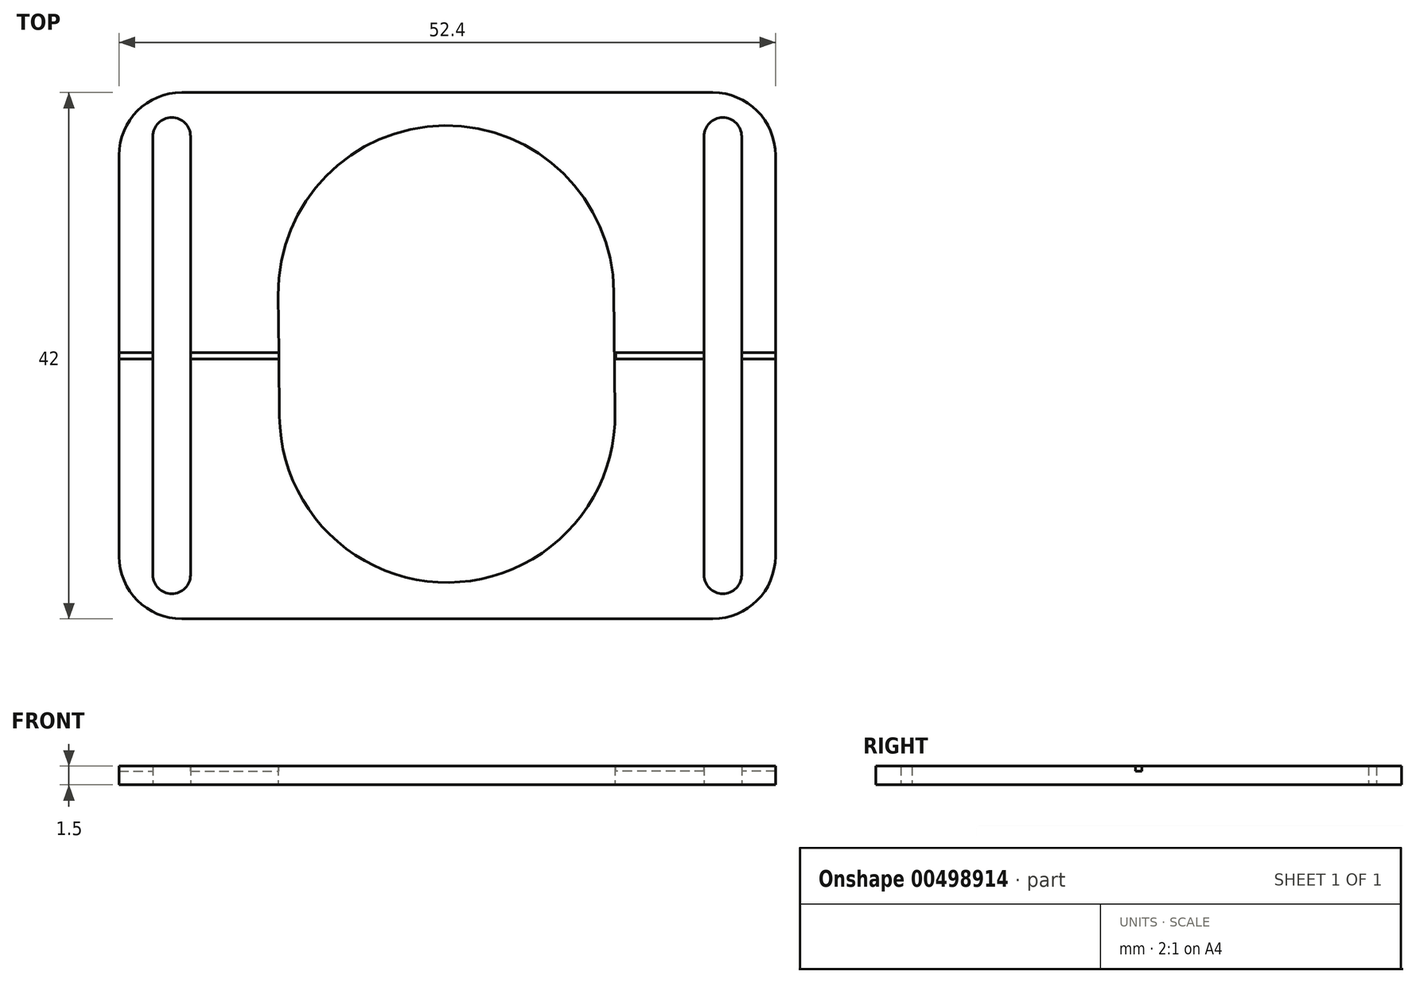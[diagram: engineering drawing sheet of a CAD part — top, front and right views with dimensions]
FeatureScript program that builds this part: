
annotation { "Feature Type Name" : "Feature", "Feature Type Description" : "" }
export const myFeature = defineFeature(function(context is Context, id is Id, definition is map)
    precondition{}
    {
        {
            var Q0;
            Q0=qCreatedBy(makeId("Top.planeOp"),FACE);
            var sketch = newSketch(context, id + "F0", { "sketchPlane" : qUnion([Q0])});
            skPoint(sketch, "E0.0", {"position": v(-35, -49.5) * mm});
            skPoint(sketch, "E1.0", {"position": v(35, -49.5) * mm});
            skLineSegment(sketch, "E2", {"start": v(-35, 25.5) * mm, "end": v(35, 25.5) * mm, "construction": true});
            skLineSegment(sketch, "E3.bottom", {"start": v(-32, -49.5) * mm, "end": v(-22, -49.5) * mm});
            skLineSegment(sketch, "E3.left", {"start": v(-35, -46.5) * mm, "end": v(-35, -44.8) * mm});
            skLineSegment(sketch, "E3.right", {"start": v(-19, -46.5) * mm, "end": v(-19, -45.44) * mm});
            skLineSegment(sketch, "E4.bottom", {"start": v(32, -49.5) * mm, "end": v(22, -49.5) * mm});
            skLineSegment(sketch, "E4.left", {"start": v(35, -46.5) * mm, "end": v(35, -44.8) * mm});
            skLineSegment(sketch, "E4.right", {"start": v(19, -46.5) * mm, "end": v(19, -45.44) * mm});
            skPoint(sketch, "E5.0", {"position": v(-19.7, -19.3) * mm});
            skPoint(sketch, "E6.0", {"position": v(19.7, -19.3) * mm});
            skArc(sketch, "E7", {"start": v(-30.65, -39.5) * mm, "mid": v(-31.62, -41.02) * mm, "end": v(-33.12, -42.02) * mm});
            skLineSegment(sketch, "E8", {"start": v(-18.8, -44.37) * mm, "end": v(-13.23, -29.76) * mm});
            skPoint(sketch, "E9.MirrorP", {"position": v(19.2, -19.2) * mm});
            skArc(sketch, "E10.MirrorCS", {"start": v(30.65, -39.5) * mm, "mid": v(31.62, -41.02) * mm, "end": v(33.12, -42.02) * mm});
            skLineSegment(sketch, "E11.MirrorCS", {"start": v(18.8, -44.37) * mm, "end": v(13.23, -29.76) * mm});
            skPoint(sketch, "E12.orphan", {"position": v(19, -39.5) * mm});
            skPoint(sketch, "E13.orphan", {"position": v(-19, -39.5) * mm});
            skPoint(sketch, "E14.visualSharp", {"position": v(-35, -42.32) * mm});
            skArc(sketch, "E14.filletArc", {"start": v(-33.12, -42.02) * mm, "mid": v(-34.48, -43.12) * mm, "end": v(-35, -44.8) * mm});
            skPoint(sketch, "E15.visualSharp", {"position": v(35, -42.32) * mm});
            skArc(sketch, "E15.filletArc", {"start": v(35, -44.8) * mm, "mid": v(34.48, -43.12) * mm, "end": v(33.12, -42.02) * mm});
            skArc(sketch, "E16.filletArc", {"start": v(32, -49.5) * mm, "mid": v(34.12, -48.62) * mm, "end": v(35, -46.5) * mm});
            skPoint(sketch, "E17.visualSharp", {"position": v(19, -49.5) * mm});
            skArc(sketch, "E17.filletArc", {"start": v(19, -46.5) * mm, "mid": v(19.88, -48.62) * mm, "end": v(22, -49.5) * mm});
            skPoint(sketch, "E18.visualSharp", {"position": v(-19, -49.5) * mm});
            skArc(sketch, "E18.filletArc", {"start": v(-22, -49.5) * mm, "mid": v(-19.88, -48.62) * mm, "end": v(-19, -46.5) * mm});
            skArc(sketch, "E19.filletArc", {"start": v(-35, -46.5) * mm, "mid": v(-34.12, -48.62) * mm, "end": v(-32, -49.5) * mm});
            skPoint(sketch, "E20.visualSharp", {"position": v(-19, -44.89) * mm});
            skArc(sketch, "E20.filletArc", {"start": v(-18.8, -44.37) * mm, "mid": v(-18.95, -44.9) * mm, "end": v(-19, -45.44) * mm});
            skPoint(sketch, "E21.visualSharp", {"position": v(19, -44.89) * mm});
            skArc(sketch, "E21.filletArc", {"start": v(19, -45.44) * mm, "mid": v(18.95, -44.9) * mm, "end": v(18.8, -44.37) * mm});
            skPoint(sketch, "E22.0", {"position": v(-32, 22.5) * mm});
            skPoint(sketch, "E23.0", {"position": v(-22, 22.5) * mm});
            skPoint(sketch, "E24.0", {"position": v(22, 22.5) * mm});
            skPoint(sketch, "E25.0", {"position": v(32, 22.5) * mm});
            skLineSegment(sketch, "E26.bottom", {"start": v(-32, 25.5) * mm, "end": v(-22, 25.5) * mm});
            skLineSegment(sketch, "E26.left", {"start": v(-35, 22.32) * mm, "end": v(-34.9, 20.58) * mm});
            skArc(sketch, "E27.filletArc", {"start": v(-34.9, 20.58) * mm, "mid": v(-34.34, 19.02) * mm, "end": v(-33.05, 18) * mm});
            skArc(sketch, "E28.filletArc", {"start": v(-32, 25.5) * mm, "mid": v(-34.18, 24.56) * mm, "end": v(-35, 22.32) * mm});
            skArc(sketch, "E29.filletArc", {"start": v(-19.63, 24.33) * mm, "mid": v(-20.68, 25.19) * mm, "end": v(-22, 25.5) * mm});
            skLineSegment(sketch, "E30", {"start": v(-33.05, 18) * mm, "end": v(-29.27, 16.41) * mm});
            skLineSegment(sketch, "E31.MirrorCS", {"start": v(35, 22.32) * mm, "end": v(34.9, 20.58) * mm});
            skArc(sketch, "E32.MirrorCS", {"start": v(19.63, 24.33) * mm, "mid": v(20.68, 25.19) * mm, "end": v(22, 25.5) * mm});
            skArc(sketch, "E33.MirrorCS", {"start": v(34.9, 20.58) * mm, "mid": v(34.34, 19.02) * mm, "end": v(33.05, 18) * mm});
            skArc(sketch, "E34.MirrorCS", {"start": v(32, 25.5) * mm, "mid": v(34.18, 24.56) * mm, "end": v(35, 22.32) * mm});
            skLineSegment(sketch, "E35.MirrorCS", {"start": v(32, 25.5) * mm, "end": v(22, 25.5) * mm});
            skLineSegment(sketch, "E36.MirrorCS", {"start": v(33.05, 18) * mm, "end": v(29.27, 16.41) * mm});
            skLineSegment(sketch, "E37", {"start": v(-15.68, 22.4) * mm, "end": v(15.68, 22.4) * mm});
            skLineSegment(sketch, "E38", {"start": v(-26.2, -26.85) * mm, "end": v(-26.2, 11.8) * mm});
            skLineSegment(sketch, "E39", {"start": v(-32, 22.5) * mm, "end": v(-22, 22.5) * mm, "construction": true});
            skCircle(sketch, "E40", {"center": v(-32, 22.5) * mm, "radius": 1.5 * mm});
            skCircle(sketch, "E41", {"center": v(32, 22.5) * mm, "radius": 1.5 * mm});
            skCircle(sketch, "E42", {"center": v(-32, -46.5) * mm, "radius": 1.5 * mm});
            skCircle(sketch, "E43", {"center": v(-22, -46.5) * mm, "radius": 1.5 * mm});
            skCircle(sketch, "E44", {"center": v(22, -46.5) * mm, "radius": 1.5 * mm});
            skCircle(sketch, "E45", {"center": v(32, -46.5) * mm, "radius": 1.5 * mm});
            skCircle(sketch, "E46", {"center": v(-22, 22.5) * mm, "radius": 1.5 * mm});
            skCircle(sketch, "E47", {"center": v(22, 22.5) * mm, "radius": 1.5 * mm});
            skCircle(sketch, "E48.0", {"center": v(-22, 0) * mm, "radius": 1.5 * mm, "construction": true});
            skCircle(sketch, "E49.0", {"center": v(-22, 10) * mm, "radius": 1.5 * mm, "construction": true});
            skCircle(sketch, "E50.0", {"center": v(-22, -10) * mm, "radius": 1.5 * mm, "construction": true});
            skArc(sketch, "E51.0.1.0", {"start": v(-23.5, -17.5) * mm, "mid": v(-22, -19) * mm, "end": v(-20.5, -17.5) * mm});
            skLineSegment(sketch, "E51.direction1", {"start": v(-22, -10) * mm, "end": v(3, -10) * mm, "construction": true});
            skLineSegment(sketch, "E51.direction2", {"start": v(-22, -10) * mm, "end": v(-22, -17.5) * mm, "construction": true});
            skArc(sketch, "E52.0.1.0", {"start": v(-20.5, 17.5) * mm, "mid": v(-22, 19) * mm, "end": v(-23.5, 17.5) * mm});
            skLineSegment(sketch, "E52.direction1", {"start": v(-22, 10) * mm, "end": v(3, 10) * mm, "construction": true});
            skLineSegment(sketch, "E52.direction2", {"start": v(-22, 10) * mm, "end": v(-22, 17.5) * mm, "construction": true});
            skLineSegment(sketch, "E53", {"start": v(-20.5, 17.5) * mm, "end": v(-20.5, -17.5) * mm});
            skLineSegment(sketch, "E54", {"start": v(-23.5, 17.5) * mm, "end": v(-23.5, -17.5) * mm});
            skArc(sketch, "E55.trimOffspring", {"start": v(-21.84, -16) * mm, "mid": v(-21.92, -16) * mm, "end": v(-22, -16) * mm});
            skLineSegment(sketch, "E56", {"start": v(-10.5, -26.94) * mm, "end": v(-3.06, -23.82) * mm});
            skLineSegment(sketch, "E57", {"start": v(3.15, -23.82) * mm, "end": v(10.5, -26.93) * mm});
            skPoint(sketch, "E58.orphan", {"position": v(-10.37, -22.5) * mm});
            skPoint(sketch, "E59.end.orphan", {"position": v(10.47, -22.53) * mm});
            skPoint(sketch, "E60.visualSharp", {"position": v(0.05, -22.51) * mm});
            skArc(sketch, "E60.filletArc", {"start": v(3.15, -23.82) * mm, "mid": v(0.05, -23.2) * mm, "end": v(-3.06, -23.82) * mm});
            skPoint(sketch, "E61.orphan", {"position": v(-26.2, 16.8) * mm});
            skPoint(sketch, "E62.trimOffspring.end.orphan", {"position": v(-19.2, 12.2) * mm});
            skLineSegment(sketch, "E63.trimOffspring", {"start": v(-26.52, -28.62) * mm, "end": v(-30.65, -39.5) * mm});
            skPoint(sketch, "E64.start.orphan", {"position": v(-19.2, -9.3) * mm});
            skPoint(sketch, "E65.trimOffspring.end.orphan", {"position": v(-9.7, -19.2) * mm});
            skPoint(sketch, "E66.orphan", {"position": v(9.2, -19.2) * mm});
            skLineSegment(sketch, "E67.MirrorCS", {"start": v(26.2, -26.85) * mm, "end": v(26.2, 11.8) * mm});
            skCircle(sketch, "E68.MirrorC", {"center": v(22, 10) * mm, "radius": 1.5 * mm, "construction": true});
            skLineSegment(sketch, "E69.MirrorCS", {"start": v(23.5, 17.5) * mm, "end": v(23.5, -17.5) * mm});
            skLineSegment(sketch, "E70.MirrorCS", {"start": v(22, -10) * mm, "end": v(22, -17.5) * mm, "construction": true});
            skLineSegment(sketch, "E71.MirrorCS", {"start": v(22, 10) * mm, "end": v(22, 17.5) * mm, "construction": true});
            skCircle(sketch, "E72.MirrorC", {"center": v(22, -10) * mm, "radius": 1.5 * mm, "construction": true});
            skArc(sketch, "E73.MirrorCS", {"start": v(20.5, 17.5) * mm, "mid": v(22, 19) * mm, "end": v(23.5, 17.5) * mm});
            skArc(sketch, "E74.MirrorCS", {"start": v(23.5, -17.5) * mm, "mid": v(22, -19) * mm, "end": v(20.5, -17.5) * mm});
            skLineSegment(sketch, "E75.MirrorCS", {"start": v(20.5, 17.5) * mm, "end": v(20.5, -17.5) * mm});
            skCircle(sketch, "E76.MirrorC", {"center": v(22, 0) * mm, "radius": 1.5 * mm, "construction": true});
            skLineSegment(sketch, "E77.trimOffspring", {"start": v(26.52, -28.62) * mm, "end": v(30.65, -39.5) * mm});
            skPoint(sketch, "E78.MirrorCS.end.orphan", {"position": v(22, -16) * mm});
            skPoint(sketch, "E78.MirrorCS.start.orphan", {"position": v(21.84, -16) * mm});
            skPoint(sketch, "E79.end.orphan", {"position": v(19.2, 12.2) * mm});
            skPoint(sketch, "E79.start.orphan", {"position": v(19.2, -9.2) * mm});
            skPoint(sketch, "E80.MirrorCS.end.orphan", {"position": v(19, 19.2) * mm});
            skPoint(sketch, "E81.MirrorCS.end.orphan", {"position": v(19, 21.46) * mm});
            skPoint(sketch, "E82.end.orphan", {"position": v(-19, 19.2) * mm});
            skPoint(sketch, "E26.right.end.orphan", {"position": v(-19, 21.46) * mm});
            skPoint(sketch, "E83.visualSharp", {"position": v(-26.2, -27.76) * mm});
            skArc(sketch, "E83.filletArc", {"start": v(-26.52, -28.62) * mm, "mid": v(-26.28, -27.75) * mm, "end": v(-26.2, -26.85) * mm});
            skPoint(sketch, "E84.visualSharp", {"position": v(26.2, -27.76) * mm});
            skArc(sketch, "E84.filletArc", {"start": v(26.2, -26.85) * mm, "mid": v(26.28, -27.75) * mm, "end": v(26.52, -28.62) * mm});
            skPoint(sketch, "E85.visualSharp", {"position": v(-12.47, -27.76) * mm});
            skArc(sketch, "E85.filletArc", {"start": v(-10.5, -26.94) * mm, "mid": v(-12.15, -28.07) * mm, "end": v(-13.23, -29.76) * mm});
            skPoint(sketch, "E86.visualSharp", {"position": v(12.47, -27.76) * mm});
            skArc(sketch, "E86.filletArc", {"start": v(13.23, -29.76) * mm, "mid": v(12.15, -28.07) * mm, "end": v(10.5, -26.93) * mm});
            skPoint(sketch, "E87.visualSharp", {"position": v(-19, 22.4) * mm});
            skArc(sketch, "E87.filletArc", {"start": v(-19.63, 24.33) * mm, "mid": v(-17.88, 22.9) * mm, "end": v(-15.68, 22.4) * mm});
            skPoint(sketch, "E88.visualSharp", {"position": v(19, 22.4) * mm});
            skArc(sketch, "E88.filletArc", {"start": v(15.68, 22.4) * mm, "mid": v(17.88, 22.9) * mm, "end": v(19.63, 24.33) * mm});
            skPoint(sketch, "E89.visualSharp", {"position": v(26.2, 15.13) * mm});
            skArc(sketch, "E89.filletArc", {"start": v(29.27, 16.41) * mm, "mid": v(27.04, 14.57) * mm, "end": v(26.2, 11.8) * mm});
            skPoint(sketch, "E90.visualSharp", {"position": v(-26.2, 15.13) * mm});
            skArc(sketch, "E90.filletArc", {"start": v(-26.2, 11.8) * mm, "mid": v(-27.04, 14.57) * mm, "end": v(-29.27, 16.41) * mm});
            skPoint(sketch, "E91.0", {"position": v(0, 0) * mm});
            skLineSegment(sketch, "E92.bottom", {"start": v(18.2, -18.2) * mm, "end": v(-18.2, -18.2) * mm});
            skLineSegment(sketch, "E92.top", {"start": v(18.2, 18.2) * mm, "end": v(-18.2, 18.2) * mm});
            skLineSegment(sketch, "E92.left", {"start": v(18.2, -18.2) * mm, "end": v(18.2, 18.2) * mm});
            skLineSegment(sketch, "E92.right", {"start": v(-18.2, -18.2) * mm, "end": v(-18.2, 18.2) * mm});
            skLineSegment(sketch, "E93.bottom", {"start": v(19.2, -19.2) * mm, "end": v(-19.2, -19.2) * mm});
            skLineSegment(sketch, "E93.top", {"start": v(19.2, 19.2) * mm, "end": v(-19.2, 19.2) * mm});
            skLineSegment(sketch, "E93.left", {"start": v(19.2, -19.2) * mm, "end": v(19.2, 19.2) * mm});
            skLineSegment(sketch, "E93.right", {"start": v(-19.2, -19.2) * mm, "end": v(-19.2, 19.2) * mm});
            skSolve(sketch);
        }
        {
            var Q0;
            Q0=qCreatedBy(makeId("Top.planeOp"),FACE);
            var sketch = newSketch(context, id + "F1", { "sketchPlane" : qUnion([Q0])});
            skCircle(sketch, "E94", {"center": v(0, 0) * mm, "radius": 12.4 * mm, "construction": true});
            skLineSegment(sketch, "E95.bottom", {"start": v(2.5, -22.4) * mm, "end": v(-2.5, -22.4) * mm, "construction": true});
            skLineSegment(sketch, "E95.top", {"start": v(2.5, 22.4) * mm, "end": v(-2.5, 22.4) * mm, "construction": true});
            skPoint(sketch, "E96", {"position": v(-22, 10) * mm});
            skCircle(sketch, "E97", {"center": v(-22, 10) * mm, "radius": 1.5 * mm, "construction": true});
            skArc(sketch, "E98.1.0.0", {"start": v(-16.7, 8.5) * mm, "mid": v(-15.2, 10) * mm, "end": v(-16.7, 11.5) * mm, "construction": true});
            skLineSegment(sketch, "E98.direction1", {"start": v(-22, 10) * mm, "end": v(-16.7, 10) * mm, "construction": true});
            skArc(sketch, "E99.1.0.0", {"start": v(-27, 11.5) * mm, "mid": v(-28.5, 10) * mm, "end": v(-27, 8.5) * mm, "construction": true});
            skLineSegment(sketch, "E99.direction1", {"start": v(-22, 10) * mm, "end": v(-27, 10) * mm, "construction": true});
            skLineSegment(sketch, "E100", {"start": v(-27, 11.5) * mm, "end": v(-16.7, 11.5) * mm, "construction": true});
            skLineSegment(sketch, "E101", {"start": v(-27, 8.5) * mm, "end": v(-16.7, 8.5) * mm, "construction": true});
            skLineSegment(sketch, "E102.direction2", {"start": v(-27, 8.5) * mm, "end": v(-27, -11.5) * mm, "construction": true});
            skPoint(sketch, "E103.visualSharp", {"position": v(-30.53, 22.4) * mm});
            skLineSegment(sketch, "E104", {"start": v(-22, 10) * mm, "end": v(-22, -10) * mm, "construction": true});
            skCircle(sketch, "E105", {"center": v(-22, 0) * mm, "radius": 1.5 * mm, "construction": true});
            skArc(sketch, "E106", {"start": v(-15.64, 4.24) * mm, "mid": v(-15.64, 6.36) * mm, "end": v(-17.76, 6.36) * mm, "construction": true});
            skLineSegment(sketch, "E107", {"start": v(-16.7, 5.3) * mm, "end": v(-22, 0) * mm, "construction": true});
            skLineSegment(sketch, "E108", {"start": v(-22, 0) * mm, "end": v(-25.5, 3.5) * mm, "construction": true});
            skArc(sketch, "E109.MirrorC", {"start": v(-26.24, -6.36) * mm, "mid": v(-28.36, -6.36) * mm, "end": v(-28.36, -4.24) * mm, "construction": true});
            skArc(sketch, "E110.MirrorC", {"start": v(-15.64, -4.24) * mm, "mid": v(-15.64, -6.36) * mm, "end": v(-17.76, -6.36) * mm, "construction": true});
            skArc(sketch, "E111.MirrorC", {"start": v(-28.36, 4.24) * mm, "mid": v(-28.36, 6.36) * mm, "end": v(-26.24, 6.36) * mm, "construction": true});
            skLineSegment(sketch, "E112", {"start": v(-26.24, 6.36) * mm, "end": v(-22.14, 2.26) * mm, "construction": true});
            skLineSegment(sketch, "E113", {"start": v(-17.76, 6.36) * mm, "end": v(-21.86, 2.26) * mm, "construction": true});
            skLineSegment(sketch, "E114.MirrorCS", {"start": v(-17.76, -6.36) * mm, "end": v(-21.86, -2.26) * mm, "construction": true});
            skLineSegment(sketch, "E115.MirrorCS", {"start": v(-26.24, -6.36) * mm, "end": v(-22.14, -2.26) * mm, "construction": true});
            skLineSegment(sketch, "E116.MirrorCS", {"start": v(-15.64, 4.24) * mm, "end": v(-19.74, 0.14) * mm, "construction": true});
            skLineSegment(sketch, "E117.MirrorCS", {"start": v(-28.36, 4.24) * mm, "end": v(-24.26, 0.14) * mm, "construction": true});
            skLineSegment(sketch, "E118.MirrorCS", {"start": v(-15.64, -4.24) * mm, "end": v(-19.74, -0.14) * mm, "construction": true});
            skLineSegment(sketch, "E119.MirrorCS", {"start": v(-28.36, -4.24) * mm, "end": v(-24.26, -0.14) * mm, "construction": true});
            skPoint(sketch, "E120.visualSharp", {"position": v(-24.12, 0) * mm});
            skArc(sketch, "E120.filletArc", {"start": v(-24.26, -0.14) * mm, "mid": v(-24.2, 0) * mm, "end": v(-24.26, 0.14) * mm, "construction": true});
            skPoint(sketch, "E121.visualSharp", {"position": v(-22, 2.12) * mm});
            skArc(sketch, "E121.filletArc", {"start": v(-22.14, 2.26) * mm, "mid": v(-22, 2.2) * mm, "end": v(-21.86, 2.26) * mm, "construction": true});
            skPoint(sketch, "E122.visualSharp", {"position": v(-19.88, 0) * mm});
            skArc(sketch, "E122.filletArc", {"start": v(-19.74, 0.14) * mm, "mid": v(-19.8, 0) * mm, "end": v(-19.74, -0.14) * mm, "construction": true});
            skPoint(sketch, "E123.visualSharp", {"position": v(-22, -2.12) * mm});
            skArc(sketch, "E123.filletArc", {"start": v(-21.86, -2.26) * mm, "mid": v(-22, -2.2) * mm, "end": v(-22.14, -2.26) * mm, "construction": true});
            skLineSegment(sketch, "E124.bottom", {"start": v(27, 13.5) * mm, "end": v(18.65, 13.5) * mm, "construction": true});
            skLineSegment(sketch, "E124.left", {"start": v(30.5, 10) * mm, "end": v(30.5, -10) * mm, "construction": true});
            skLineSegment(sketch, "E124.right", {"start": v(-30.5, 10) * mm, "end": v(-30.5, -10) * mm, "construction": true});
            skArc(sketch, "E125.MirrorCS", {"start": v(22.14, 2.26) * mm, "mid": v(22, 2.2) * mm, "end": v(21.86, 2.26) * mm, "construction": true});
            skArc(sketch, "E126.MirrorCS", {"start": v(21.86, -2.26) * mm, "mid": v(22, -2.2) * mm, "end": v(22.14, -2.26) * mm, "construction": true});
            skArc(sketch, "E127.MirrorCS", {"start": v(19.74, 0.14) * mm, "mid": v(19.8, 0) * mm, "end": v(19.74, -0.14) * mm, "construction": true});
            skArc(sketch, "E128.MirrorCS", {"start": v(24.26, -0.14) * mm, "mid": v(24.2, 0) * mm, "end": v(24.26, 0.14) * mm, "construction": true});
            skPoint(sketch, "E129.MirrorP", {"position": v(24.12, 0) * mm});
            skLineSegment(sketch, "E130.MirrorCS", {"start": v(15.64, -4.24) * mm, "end": v(19.74, -0.14) * mm, "construction": true});
            skArc(sketch, "E131.MirrorCS", {"start": v(28.36, 4.24) * mm, "mid": v(28.36, 6.36) * mm, "end": v(26.24, 6.36) * mm, "construction": true});
            skPoint(sketch, "E132.MirrorP", {"position": v(22, -2.12) * mm});
            skPoint(sketch, "E133.MirrorP", {"position": v(22, 2.12) * mm});
            skLineSegment(sketch, "E134.MirrorCS", {"start": v(22, 0) * mm, "end": v(25.5, 3.5) * mm, "construction": true});
            skArc(sketch, "E135.MirrorCS", {"start": v(15.64, -4.24) * mm, "mid": v(15.64, -6.36) * mm, "end": v(17.76, -6.36) * mm, "construction": true});
            skLineSegment(sketch, "E136.MirrorCS", {"start": v(28.36, 4.24) * mm, "end": v(24.26, 0.14) * mm, "construction": true});
            skPoint(sketch, "E137.MirrorP", {"position": v(22, 10) * mm});
            skArc(sketch, "E138.MirrorCS", {"start": v(16.7, 8.5) * mm, "mid": v(15.2, 10) * mm, "end": v(16.7, 11.5) * mm, "construction": true});
            skArc(sketch, "E139.MirrorCS", {"start": v(27, 11.5) * mm, "mid": v(28.5, 10) * mm, "end": v(27, 8.5) * mm, "construction": true});
            skLineSegment(sketch, "E140.MirrorCS", {"start": v(27, 8.5) * mm, "end": v(16.7, 8.5) * mm, "construction": true});
            skLineSegment(sketch, "E141.MirrorCS", {"start": v(28.36, -4.24) * mm, "end": v(24.26, -0.14) * mm, "construction": true});
            skPoint(sketch, "E142.MirrorP", {"position": v(19.88, 0) * mm});
            skArc(sketch, "E143.MirrorCS", {"start": v(15.64, 4.24) * mm, "mid": v(15.64, 6.36) * mm, "end": v(17.76, 6.36) * mm, "construction": true});
            skLineSegment(sketch, "E144.MirrorCS", {"start": v(27, 8.5) * mm, "end": v(27, -11.5) * mm, "construction": true});
            skLineSegment(sketch, "E145.MirrorCS", {"start": v(15.64, 4.24) * mm, "end": v(19.74, 0.14) * mm, "construction": true});
            skArc(sketch, "E146.MirrorCS", {"start": v(26.24, -6.36) * mm, "mid": v(28.36, -6.36) * mm, "end": v(28.36, -4.24) * mm, "construction": true});
            skLineSegment(sketch, "E147.MirrorCS", {"start": v(22, 10) * mm, "end": v(16.7, 10) * mm, "construction": true});
            skLineSegment(sketch, "E148.MirrorCS", {"start": v(22, 10) * mm, "end": v(22, -10) * mm, "construction": true});
            skCircle(sketch, "E149.MirrorC", {"center": v(22, 10) * mm, "radius": 1.5 * mm, "construction": true});
            skLineSegment(sketch, "E150.MirrorCS", {"start": v(16.7, 5.3) * mm, "end": v(22, 0) * mm, "construction": true});
            skLineSegment(sketch, "E151.MirrorCS", {"start": v(17.76, -6.36) * mm, "end": v(21.86, -2.26) * mm, "construction": true});
            skCircle(sketch, "E152.MirrorC", {"center": v(22, 0) * mm, "radius": 1.5 * mm, "construction": true});
            skLineSegment(sketch, "E153.MirrorCS", {"start": v(27, 11.5) * mm, "end": v(16.7, 11.5) * mm, "construction": true});
            skLineSegment(sketch, "E154.MirrorCS", {"start": v(26.24, 6.36) * mm, "end": v(22.14, 2.26) * mm, "construction": true});
            skLineSegment(sketch, "E155.MirrorCS", {"start": v(22, 10) * mm, "end": v(27, 10) * mm, "construction": true});
            skLineSegment(sketch, "E156.MirrorCS", {"start": v(26.24, -6.36) * mm, "end": v(22.14, -2.26) * mm, "construction": true});
            skLineSegment(sketch, "E157.MirrorCS", {"start": v(17.76, 6.36) * mm, "end": v(21.86, 2.26) * mm, "construction": true});
            skFitSpline(sketch, "E158", {"points": [v(-18.65, 13.5) * mm, v(-13.06, 15.7) * mm, v(-10.09, 18.6) * mm, v(-2.5, 22.4) * mm], "startDerivative": vector(19.72, -0.07) * mm, "endDerivative": vector(26.63, 0) * mm, "construction": true});
            skFitSpline(sketch, "E159.MirrorCS", {"points": [v(18.65, 13.5) * mm, v(13.06, 15.7) * mm, v(10.09, 18.6) * mm, v(2.5, 22.4) * mm], "startDerivative": vector(-19.72, -0.07) * mm, "endDerivative": vector(-26.63, 0) * mm, "construction": true});
            skFitSpline(sketch, "E160.MirrorCS", {"points": [v(-18.65, -13.5) * mm, v(-13.06, -15.7) * mm, v(-10.09, -18.6) * mm, v(-2.5, -22.4) * mm], "startDerivative": vector(19.72, 0.07) * mm, "endDerivative": vector(26.63, 0) * mm, "construction": true});
            skFitSpline(sketch, "E161.MirrorCS", {"points": [v(18.65, -13.5) * mm, v(13.06, -15.7) * mm, v(10.09, -18.6) * mm, v(2.5, -22.4) * mm], "startDerivative": vector(-19.72, 0.07) * mm, "endDerivative": vector(-26.63, 0) * mm, "construction": true});
            skPoint(sketch, "E162.visualSharp", {"position": v(-30.5, -13.5) * mm});
            skArc(sketch, "E162.filletArc", {"start": v(-30.5, -10) * mm, "mid": v(-29.5, -12.45) * mm, "end": v(-27.07, -13.5) * mm, "construction": true});
            skArc(sketch, "E163.filletArc", {"start": v(-27.15, 13.5) * mm, "mid": v(-29.53, 12.42) * mm, "end": v(-30.5, 10) * mm, "construction": true});
            skPoint(sketch, "E164.visualSharp", {"position": v(30.5, -13.5) * mm});
            skArc(sketch, "E164.filletArc", {"start": v(27.08, -13.5) * mm, "mid": v(29.5, -12.45) * mm, "end": v(30.5, -10) * mm, "construction": true});
            skPoint(sketch, "E165.visualSharp", {"position": v(30.5, 13.5) * mm});
            skArc(sketch, "E165.filletArc", {"start": v(30.5, 10) * mm, "mid": v(29.47, 12.47) * mm, "end": v(27, 13.5) * mm, "construction": true});
            skCircle(sketch, "E166.MirrorC", {"center": v(22, -10) * mm, "radius": 1.5 * mm, "construction": true});
            skArc(sketch, "E167.MirrorCS", {"start": v(27, -11.5) * mm, "mid": v(28.5, -10) * mm, "end": v(27, -8.5) * mm, "construction": true});
            skLineSegment(sketch, "E168.MirrorCS", {"start": v(22, -10) * mm, "end": v(27, -10) * mm, "construction": true});
            skLineSegment(sketch, "E169.MirrorCS", {"start": v(27, -8.5) * mm, "end": v(16.7, -8.5) * mm, "construction": true});
            skLineSegment(sketch, "E170.MirrorCS", {"start": v(27, -11.5) * mm, "end": v(16.7, -11.5) * mm, "construction": true});
            skLineSegment(sketch, "E171.MirrorCS", {"start": v(22, -10) * mm, "end": v(16.7, -10) * mm, "construction": true});
            skArc(sketch, "E172.MirrorCS", {"start": v(16.7, -8.5) * mm, "mid": v(15.2, -10) * mm, "end": v(16.7, -11.5) * mm, "construction": true});
            skArc(sketch, "E173.MirrorCS", {"start": v(-27, -11.5) * mm, "mid": v(-28.5, -10) * mm, "end": v(-27, -8.5) * mm, "construction": true});
            skLineSegment(sketch, "E174.MirrorCS", {"start": v(-27, -11.5) * mm, "end": v(-16.7, -11.5) * mm, "construction": true});
            skLineSegment(sketch, "E175.MirrorCS", {"start": v(-27, -8.5) * mm, "end": v(-16.7, -8.5) * mm, "construction": true});
            skArc(sketch, "E176.MirrorCS", {"start": v(-16.7, -8.5) * mm, "mid": v(-15.2, -10) * mm, "end": v(-16.7, -11.5) * mm, "construction": true});
            skLineSegment(sketch, "E177.MirrorCS", {"start": v(-22, -10) * mm, "end": v(-27, -10) * mm, "construction": true});
            skLineSegment(sketch, "E178.MirrorCS", {"start": v(-22, -10) * mm, "end": v(-16.7, -10) * mm, "construction": true});
            skCircle(sketch, "E179.MirrorC", {"center": v(-22, -10) * mm, "radius": 1.5 * mm, "construction": true});
            skLineSegment(sketch, "E180", {"start": v(-27.15, 13.5) * mm, "end": v(-18.65, 13.5) * mm, "construction": true});
            skLineSegment(sketch, "E181", {"start": v(27.08, -13.5) * mm, "end": v(18.65, -13.5) * mm, "construction": true});
            skLineSegment(sketch, "E182", {"start": v(-27.07, -13.5) * mm, "end": v(-18.65, -13.5) * mm, "construction": true});
            skSolve(sketch);
        }
        {
            var Q0;
            Q0=qCreatedBy(makeId("Top.planeOp"),FACE);
            var sketch = newSketch(context, id + "F2", { "sketchPlane" : qUnion([Q0])});
            skLineSegment(sketch, "E183.0.0", {"start": v(-20.5, -17.5) * mm, "end": v(-20.5, 17.5) * mm});
            skArc(sketch, "E183.0.1", {"start": v(-20.5, 17.5) * mm, "mid": v(-22, 19) * mm, "end": v(-23.5, 17.5) * mm});
            skLineSegment(sketch, "E183.0.2", {"start": v(-23.5, 17.5) * mm, "end": v(-23.5, -17.5) * mm});
            skArc(sketch, "E183.0.3", {"start": v(-23.5, -17.5) * mm, "mid": v(-22, -19) * mm, "end": v(-20.5, -17.5) * mm});
            skArc(sketch, "E184.0.0", {"start": v(23.5, 17.5) * mm, "mid": v(22, 19) * mm, "end": v(20.5, 17.5) * mm});
            skLineSegment(sketch, "E184.0.1", {"start": v(20.5, 17.5) * mm, "end": v(20.5, -17.5) * mm});
            skArc(sketch, "E184.0.2", {"start": v(20.5, -17.5) * mm, "mid": v(22, -19) * mm, "end": v(23.5, -17.5) * mm});
            skLineSegment(sketch, "E184.0.3", {"start": v(23.5, -17.5) * mm, "end": v(23.5, 17.5) * mm});
            skLineSegment(sketch, "E185.bottom", {"start": v(21.2, 21) * mm, "end": v(-21.2, 21) * mm});
            skLineSegment(sketch, "E185.top", {"start": v(21.2, -21) * mm, "end": v(-21.2, -21) * mm});
            skLineSegment(sketch, "E185.left", {"start": v(26.2, 16) * mm, "end": v(26.2, -16) * mm});
            skLineSegment(sketch, "E185.right", {"start": v(-26.2, 16) * mm, "end": v(-26.2, -16) * mm});
            skPoint(sketch, "E185.middle", {"position": v(0, 0) * mm});
            skPoint(sketch, "E186.visualSharp", {"position": v(-26.2, 21) * mm});
            skArc(sketch, "E186.filletArc", {"start": v(-21.2, 21) * mm, "mid": v(-24.74, 19.54) * mm, "end": v(-26.2, 16) * mm});
            skPoint(sketch, "E187.visualSharp", {"position": v(26.2, 21) * mm});
            skArc(sketch, "E187.filletArc", {"start": v(26.2, 16) * mm, "mid": v(24.74, 19.54) * mm, "end": v(21.2, 21) * mm});
            skPoint(sketch, "E188.visualSharp", {"position": v(26.2, -21) * mm});
            skArc(sketch, "E188.filletArc", {"start": v(21.2, -21) * mm, "mid": v(24.74, -19.54) * mm, "end": v(26.2, -16) * mm});
            skPoint(sketch, "E189.visualSharp", {"position": v(-26.2, -21) * mm});
            skArc(sketch, "E189.filletArc", {"start": v(-26.2, -16) * mm, "mid": v(-24.74, -19.54) * mm, "end": v(-21.2, -21) * mm});
            skCircle(sketch, "E190.0", {"center": v(0, 0) * mm, "radius": 12.4 * mm, "construction": true});
            skCircle(sketch, "E191", {"center": v(0, 0) * mm, "radius": 13.4 * mm, "construction": true});
            skArc(sketch, "E192", {"start": v(13.3, 5.1) * mm, "mid": v(-0.24, 18.36) * mm, "end": v(-13.5, 4.82) * mm});
            skArc(sketch, "E193", {"start": v(-13.4, -4.84) * mm, "mid": v(0.14, -18.1) * mm, "end": v(13.4, -4.56) * mm});
            skLineSegment(sketch, "E194", {"start": v(-13.5, 4.82) * mm, "end": v(-13.4, -4.84) * mm});
            skLineSegment(sketch, "E195", {"start": v(13.3, 5.1) * mm, "end": v(13.4, -4.56) * mm});
            skSolve(sketch);
        }
        {
            var Q0;
            Q0=makeQuery(id+"F2.imprint","IMPRINT",FACE,{"disambiguationData":[TD([[makeQuery(id+"F2.imprint","IMPRINT",EDGE,{"derivedFrom":sQuery(id+"F2.wireOp",EDGE,"E183.0.0")}),-1.0]])]});
            extrude(context, id + "F3", {"entities" : qUnion([Q0]), "depth" : 1.5 * mm});
        }
        {
            var Q0;
            Q0=makeQuery(id+"F3.opExtrude","CAP_FACE",FACE,{"disambiguationData":[OSD([sQuery(id+"F2.wireOp",EDGE,"E183.0.0"),sQuery(id+"F2.wireOp",EDGE,"E183.0.1"),sQuery(id+"F2.wireOp",EDGE,"E183.0.2"),sQuery(id+"F2.wireOp",EDGE,"E183.0.3"),sQuery(id+"F2.wireOp",EDGE,"E184.0.0"),sQuery(id+"F2.wireOp",EDGE,"E184.0.1"),sQuery(id+"F2.wireOp",EDGE,"E184.0.2"),sQuery(id+"F2.wireOp",EDGE,"E184.0.3"),sQuery(id+"F2.wireOp",EDGE,"E185.bottom"),sQuery(id+"F2.wireOp",EDGE,"E185.top"),sQuery(id+"F2.wireOp",EDGE,"E185.left"),sQuery(id+"F2.wireOp",EDGE,"E185.right"),sQuery(id+"F2.wireOp",EDGE,"E186.filletArc"),sQuery(id+"F2.wireOp",EDGE,"E187.filletArc"),sQuery(id+"F2.wireOp",EDGE,"E188.filletArc"),sQuery(id+"F2.wireOp",EDGE,"E189.filletArc"),sQuery(id+"F2.wireOp",EDGE,"E192"),sQuery(id+"F2.wireOp",EDGE,"E193"),sQuery(id+"F2.wireOp",EDGE,"E194"),sQuery(id+"F2.wireOp",EDGE,"E195")])],"isStart":false});
            var sketch = newSketch(context, id + "F4", { "sketchPlane" : qUnion([Q0])});
            skLineSegment(sketch, "E196.bottom", {"start": v(-26.2, 0.25) * mm, "end": v(-13.45, 0.25) * mm});
            skLineSegment(sketch, "E196.top", {"start": v(-26.2, -0.25) * mm, "end": v(-13.45, -0.25) * mm});
            skLineSegment(sketch, "E196.left", {"start": v(-26.2, 0.25) * mm, "end": v(-26.2, -0.25) * mm});
            skLineSegment(sketch, "E196.right", {"start": v(-13.45, 0.25) * mm, "end": v(-13.45, -0.25) * mm});
            skLineSegment(sketch, "E197.MirrorCS", {"start": v(13.45, 0.25) * mm, "end": v(13.45, -0.25) * mm});
            skLineSegment(sketch, "E198.MirrorCS", {"start": v(26.2, 0.25) * mm, "end": v(26.2, -0.25) * mm});
            skLineSegment(sketch, "E199.MirrorCS", {"start": v(26.2, 0.25) * mm, "end": v(13.45, 0.25) * mm});
            skLineSegment(sketch, "E200.MirrorCS", {"start": v(26.2, -0.25) * mm, "end": v(13.45, -0.25) * mm});
            skSolve(sketch);
        }
        {
            var Q0;
            Q0 = qSketchRegion(id + "F4", true);
            extrude(context, id + "F5", {"entities" : qUnion([Q0]), "operationType" : NewBodyOperationType.REMOVE, "oppositeDirection" : true, "depth" : 0.4 * mm, "offsetDistance" : 25 * mm});
        }
    });
